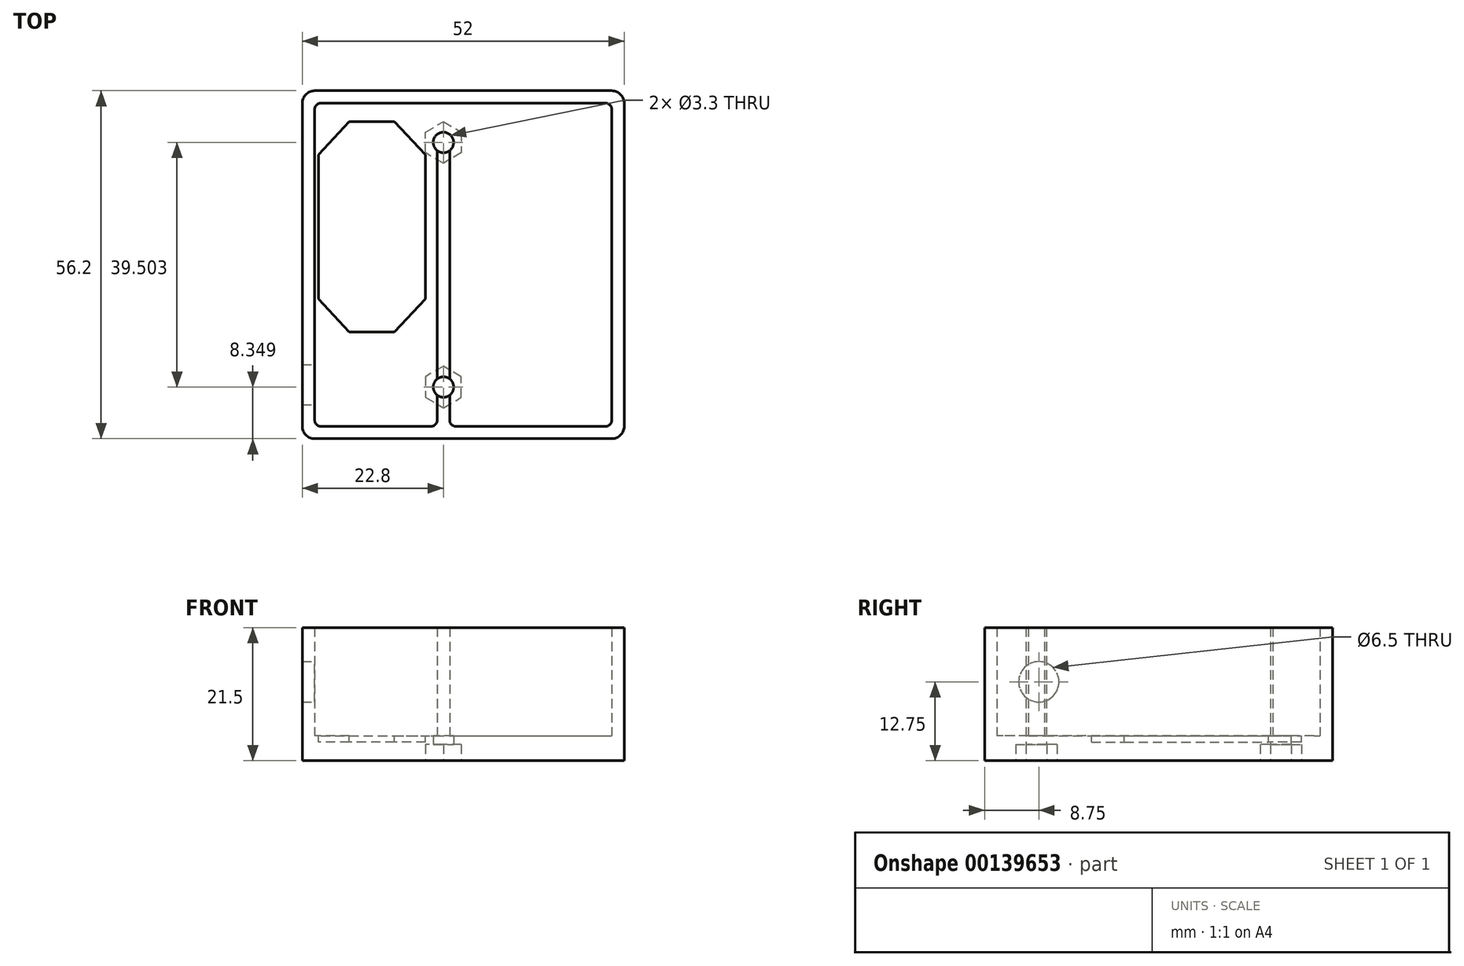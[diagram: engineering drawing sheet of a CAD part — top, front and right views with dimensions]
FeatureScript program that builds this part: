
annotation { "Feature Type Name" : "Feature", "Feature Type Description" : "" }
export const myFeature = defineFeature(function(context is Context, id is Id, definition is map)
    precondition{}
    {
        {
            var Q0;
            Q0=qCreatedBy(makeId("Top.planeOp"),FACE);
            var sketch = newSketch(context, id + "F0", { "sketchPlane" : qUnion([Q0])});
            skLineSegment(sketch, "E0.bottom", {"start": v(0, 0) * mm, "end": v(52, 0) * mm});
            skLineSegment(sketch, "E0.top", {"start": v(0, 56.2) * mm, "end": v(52, 56.2) * mm});
            skLineSegment(sketch, "E0.left", {"start": v(0, 0) * mm, "end": v(0, 56.2) * mm});
            skLineSegment(sketch, "E0.right", {"start": v(52, 0) * mm, "end": v(52, 56.2) * mm});
            skSolve(sketch);
        }
        {
            var Q0;
            Q0 = qSketchRegion(id + "F0", true);
            extrude(context, id + "F1", {"entities" : qUnion([Q0]), "depth" : 4 * mm});
        }
        {
            var Q0;
            Q0=makeQuery(id+"F1.opExtrude","CAP_FACE",FACE,{"disambiguationData":[OSD([sQuery(id+"F0.wireOp",EDGE,"E0.bottom"),sQuery(id+"F0.wireOp",EDGE,"E0.top"),sQuery(id+"F0.wireOp",EDGE,"E0.left"),sQuery(id+"F0.wireOp",EDGE,"E0.right")])],"isStart":false});
            var sketch = newSketch(context, id + "F2", { "sketchPlane" : qUnion([Q0])});
            skLineSegment(sketch, "E1.bottom", {"start": v(0, 56.2) * mm, "end": v(52, 56.2) * mm});
            skLineSegment(sketch, "E1.top", {"start": v(0, 0) * mm, "end": v(52, 0) * mm});
            skLineSegment(sketch, "E1.left", {"start": v(0, 56.2) * mm, "end": v(0, 0) * mm});
            skLineSegment(sketch, "E1.right", {"start": v(52, 56.2) * mm, "end": v(52, 0) * mm});
            skLineSegment(sketch, "E2.bottom", {"start": v(2, 54.2) * mm, "end": v(50, 54.2) * mm});
            skLineSegment(sketch, "E2.top", {"start": v(2, 2) * mm, "end": v(21.8, 2) * mm});
            skLineSegment(sketch, "E2.left", {"start": v(2, 54.2) * mm, "end": v(2, 2) * mm});
            skLineSegment(sketch, "E2.right", {"start": v(50, 54.2) * mm, "end": v(50, 2) * mm});
            skLineSegment(sketch, "E3", {"start": v(21.8, 2) * mm, "end": v(21.8, 48.2) * mm});
            skLineSegment(sketch, "E4", {"start": v(21.8, 48.2) * mm, "end": v(23.8, 48.2) * mm});
            skLineSegment(sketch, "E5", {"start": v(23.8, 48.2) * mm, "end": v(23.8, 2) * mm});
            skLineSegment(sketch, "E6.trimOffspring", {"start": v(23.8, 2) * mm, "end": v(50, 2) * mm});
            skSolve(sketch);
        }
        {
            var Q0;
            Q0 = qSketchRegion(id + "F2", true);
            extrude(context, id + "F3", {"entities" : qUnion([Q0]), "operationType" : NewBodyOperationType.ADD, "depth" : 17.5 * mm});
        }
        {
            var Q0;
            Q0=makeQuery(id+"F1.opExtrude","CAP_FACE",FACE,{"disambiguationData":[OSD([sQuery(id+"F0.wireOp",EDGE,"E0.bottom"),sQuery(id+"F0.wireOp",EDGE,"E0.top"),sQuery(id+"F0.wireOp",EDGE,"E0.left"),sQuery(id+"F0.wireOp",EDGE,"E0.right")])],"isStart":false});
            var sketch = newSketch(context, id + "F4", { "sketchPlane" : qUnion([Q0])});
            skLineSegment(sketch, "E7", {"start": v(2.6, 22.58) * mm, "end": v(2.6, 45.88) * mm});
            skLineSegment(sketch, "E8", {"start": v(2.6, 45.88) * mm, "end": v(7.6, 51.2) * mm});
            skLineSegment(sketch, "E9", {"start": v(7.6, 51.2) * mm, "end": v(14.9, 51.2) * mm});
            skLineSegment(sketch, "E10", {"start": v(14.9, 51.2) * mm, "end": v(19.9, 45.88) * mm});
            skLineSegment(sketch, "E11", {"start": v(19.9, 45.88) * mm, "end": v(19.9, 22.58) * mm});
            skLineSegment(sketch, "E12", {"start": v(19.9, 22.58) * mm, "end": v(14.9, 17.26) * mm});
            skLineSegment(sketch, "E13", {"start": v(14.9, 17.26) * mm, "end": v(7.6, 17.26) * mm});
            skLineSegment(sketch, "E14", {"start": v(7.6, 17.26) * mm, "end": v(2.6, 22.58) * mm});
            skLineSegment(sketch, "E15", {"start": v(2.6, 45.88) * mm, "end": v(19.9, 45.88) * mm, "construction": true});
            skSolve(sketch);
        }
        {
            var Q0;
            Q0 = qSketchRegion(id + "F4", true);
            extrude(context, id + "F5", {"entities" : qUnion([Q0]), "operationType" : NewBodyOperationType.REMOVE, "oppositeDirection" : true, "depth" : 1 * mm});
        }
        {
            var Q0;
            Q0=makeQuery(id+"F3.opExtrude","SWEPT_FACE",FACE,{"disambiguationData":[OSD([sQuery(id+"F2.wireOp",EDGE,"E2.left")])]});
            var sketch = newSketch(context, id + "F6", { "sketchPlane" : qUnion([Q0])});
            skCircle(sketch, "E16", {"center": v(8.75, 12.75) * mm, "radius": 3.25 * mm});
            skSolve(sketch);
        }
        {
            var Q0;
            Q0 = qSketchRegion(id + "F6", true);
            extrude(context, id + "F7", {"entities" : qUnion([Q0]), "operationType" : NewBodyOperationType.REMOVE, "endBound" : BoundingType.UP_TO_NEXT, "oppositeDirection" : true, "depth" : 25 * mm});
        }
        {
            var Q0;
            Q0=makeQuery(id+"F1.opExtrude","CAP_FACE",FACE,{"disambiguationData":[OSD([sQuery(id+"F0.wireOp",EDGE,"E0.bottom"),sQuery(id+"F0.wireOp",EDGE,"E0.top"),sQuery(id+"F0.wireOp",EDGE,"E0.left"),sQuery(id+"F0.wireOp",EDGE,"E0.right")])],"isStart":true});
            var sketch = newSketch(context, id + "F8", { "sketchPlane" : qUnion([Q0])});
            skCircle(sketch, "E17.cCircle", {"center": v(22.8, -8.35) * mm, "radius": 2.9 * mm, "construction": true});
            skLineSegment(sketch, "E17.0", {"start": v(22.8, -11.7) * mm, "end": v(19.9, -10.02) * mm});
            skLineSegment(sketch, "E17.1", {"start": v(19.9, -10.02) * mm, "end": v(19.9, -6.67) * mm});
            skLineSegment(sketch, "E17.2", {"start": v(19.9, -6.67) * mm, "end": v(22.8, -5) * mm});
            skLineSegment(sketch, "E17.3", {"start": v(22.8, -5) * mm, "end": v(25.7, -6.67) * mm});
            skLineSegment(sketch, "E17.4", {"start": v(25.7, -6.67) * mm, "end": v(25.7, -10.02) * mm});
            skLineSegment(sketch, "E17.5", {"start": v(25.7, -10.02) * mm, "end": v(22.8, -11.7) * mm});
            skPoint(sketch, "E17.0.midPoint", {"position": v(21.35, -10.86) * mm});
            skLineSegment(sketch, "E18", {"start": v(0, -28.1) * mm, "end": v(52, -28.1) * mm, "construction": true});
            skLineSegment(sketch, "E19.MirrorCS", {"start": v(19.9, -46.18) * mm, "end": v(19.9, -49.53) * mm});
            skLineSegment(sketch, "E20.MirrorCS", {"start": v(25.7, -46.18) * mm, "end": v(22.8, -44.5) * mm});
            skLineSegment(sketch, "E21.MirrorCS", {"start": v(25.7, -49.53) * mm, "end": v(25.7, -46.18) * mm});
            skLineSegment(sketch, "E22.MirrorCS", {"start": v(19.9, -49.53) * mm, "end": v(22.8, -51.2) * mm});
            skLineSegment(sketch, "E23.MirrorCS", {"start": v(22.8, -44.5) * mm, "end": v(19.9, -46.18) * mm});
            skCircle(sketch, "E24.MirrorC", {"center": v(22.8, -47.85) * mm, "radius": 2.9 * mm, "construction": true});
            skLineSegment(sketch, "E25.MirrorCS", {"start": v(22.8, -51.2) * mm, "end": v(25.7, -49.53) * mm});
            skPoint(sketch, "E26.MirrorP", {"position": v(21.35, -45.34) * mm});
            skSolve(sketch);
        }
        {
            var Q0;
            Q0 = qSketchRegion(id + "F8", true);
            extrude(context, id + "F9", {"entities" : qUnion([Q0]), "operationType" : NewBodyOperationType.REMOVE, "oppositeDirection" : true, "depth" : 2.6 * mm});
        }
        {
            var Q0;
            Q0=makeQuery(id+"F1.opExtrude","CAP_FACE",FACE,{"disambiguationData":[OSD([sQuery(id+"F0.wireOp",EDGE,"E0.bottom"),sQuery(id+"F0.wireOp",EDGE,"E0.top"),sQuery(id+"F0.wireOp",EDGE,"E0.left"),sQuery(id+"F0.wireOp",EDGE,"E0.right")])],"isStart":true});
            var sketch = newSketch(context, id + "F10", { "sketchPlane" : qUnion([Q0])});
            skLineSegment(sketch, "E27", {"start": v(22.8, -44.5) * mm, "end": v(22.8, -51.2) * mm, "construction": true});
            skCircle(sketch, "E28", {"center": v(22.8, -47.85) * mm, "radius": 1.65 * mm});
            skLineSegment(sketch, "E29", {"start": v(0, -28.1) * mm, "end": v(52, -28.1) * mm, "construction": true});
            skLineSegment(sketch, "E30.MirrorCS", {"start": v(22.8, -11.7) * mm, "end": v(22.8, -5) * mm, "construction": true});
            skCircle(sketch, "E31.MirrorC", {"center": v(22.8, -8.35) * mm, "radius": 1.65 * mm});
            skSolve(sketch);
        }
        {
            var Q0;
            Q0 = qSketchRegion(id + "F10", true);
            extrude(context, id + "F11", {"entities" : qUnion([Q0]), "operationType" : NewBodyOperationType.REMOVE, "endBound" : BoundingType.THROUGH_ALL, "oppositeDirection" : true, "depth" : 25 * mm});
        }
        {
            var Q0;
            Q0=makeQuery(id+"F3.boolean.opBoolean","MERGE",EDGE,{"derivedFrom":[makeQuery(id+"F1.opExtrude","SWEPT_EDGE",EDGE,{"disambiguationData":[OSD([sQuery(id+"F0.wireOp",EDGE,"E0.bottom"),sQuery(id+"F0.wireOp",EDGE,"E0.left")])]}),makeQuery(id+"F3.opExtrude","SWEPT_EDGE",EDGE,{"disambiguationData":[OSD([sQuery(id+"F2.wireOp",EDGE,"E1.top"),sQuery(id+"F2.wireOp",EDGE,"E1.left")])]})]});
            var Q1;
            Q1=makeQuery(id+"F3.boolean.opBoolean","MERGE",EDGE,{"derivedFrom":[makeQuery(id+"F1.opExtrude","SWEPT_EDGE",EDGE,{"disambiguationData":[OSD([sQuery(id+"F0.wireOp",EDGE,"E0.bottom"),sQuery(id+"F0.wireOp",EDGE,"E0.right")])]}),makeQuery(id+"F3.opExtrude","SWEPT_EDGE",EDGE,{"disambiguationData":[OSD([sQuery(id+"F2.wireOp",EDGE,"E1.top"),sQuery(id+"F2.wireOp",EDGE,"E1.right")])]})]});
            var Q2;
            Q2=makeQuery(id+"F3.boolean.opBoolean","MERGE",EDGE,{"derivedFrom":[makeQuery(id+"F1.opExtrude","SWEPT_EDGE",EDGE,{"disambiguationData":[OSD([sQuery(id+"F0.wireOp",EDGE,"E0.top"),sQuery(id+"F0.wireOp",EDGE,"E0.left")])]}),makeQuery(id+"F3.opExtrude","SWEPT_EDGE",EDGE,{"disambiguationData":[OSD([sQuery(id+"F2.wireOp",EDGE,"E1.bottom"),sQuery(id+"F2.wireOp",EDGE,"E1.left")])]})]});
            var Q3;
            Q3=makeQuery(id+"F3.boolean.opBoolean","MERGE",EDGE,{"derivedFrom":[makeQuery(id+"F1.opExtrude","SWEPT_EDGE",EDGE,{"disambiguationData":[OSD([sQuery(id+"F0.wireOp",EDGE,"E0.top"),sQuery(id+"F0.wireOp",EDGE,"E0.right")])]}),makeQuery(id+"F3.opExtrude","SWEPT_EDGE",EDGE,{"disambiguationData":[OSD([sQuery(id+"F2.wireOp",EDGE,"E1.bottom"),sQuery(id+"F2.wireOp",EDGE,"E1.right")])]})]});
            fillet(context, id + "F12", {"entities" : qUnion([Q0, Q1, Q2, Q3]), "radius" : 2 * mm, "tangentPropagation" : true, "allowEdgeOverflow" : false});
        }
        {
            var Q0;
            Q0=makeQuery(id+"F3.opExtrude","SWEPT_EDGE",EDGE,{"disambiguationData":[OSD([sQuery(id+"F2.wireOp",EDGE,"E2.bottom"),sQuery(id+"F2.wireOp",EDGE,"E2.right")])]});
            var Q1;
            Q1=makeQuery(id+"F3.opExtrude","SWEPT_EDGE",EDGE,{"disambiguationData":[OSD([sQuery(id+"F2.wireOp",EDGE,"E2.right"),sQuery(id+"F2.wireOp",EDGE,"E6.trimOffspring")])]});
            var Q2;
            Q2=makeQuery(id+"F3.opExtrude","SWEPT_EDGE",EDGE,{"disambiguationData":[OSD([sQuery(id+"F2.wireOp",EDGE,"E2.top"),sQuery(id+"F2.wireOp",EDGE,"E2.left")])]});
            var Q3;
            Q3=makeQuery(id+"F3.opExtrude","SWEPT_EDGE",EDGE,{"disambiguationData":[OSD([sQuery(id+"F2.wireOp",EDGE,"E2.bottom"),sQuery(id+"F2.wireOp",EDGE,"E2.left")])]});
            var Q4;
            Q4=makeQuery(id+"F3.opExtrude","SWEPT_EDGE",EDGE,{"disambiguationData":[OSD([sQuery(id+"F2.wireOp",EDGE,"E2.top"),sQuery(id+"F2.wireOp",EDGE,"E3")])]});
            var Q5;
            Q5=makeQuery(id+"F3.opExtrude","SWEPT_EDGE",EDGE,{"disambiguationData":[OSD([sQuery(id+"F2.wireOp",EDGE,"E5"),sQuery(id+"F2.wireOp",EDGE,"E6.trimOffspring")])]});
            fillet(context, id + "F13", {"entities" : qUnion([Q0, Q1, Q2, Q3, Q4, Q5]), "radius" : 1 * mm, "tangentPropagation" : true, "allowEdgeOverflow" : false});
        }
    });
